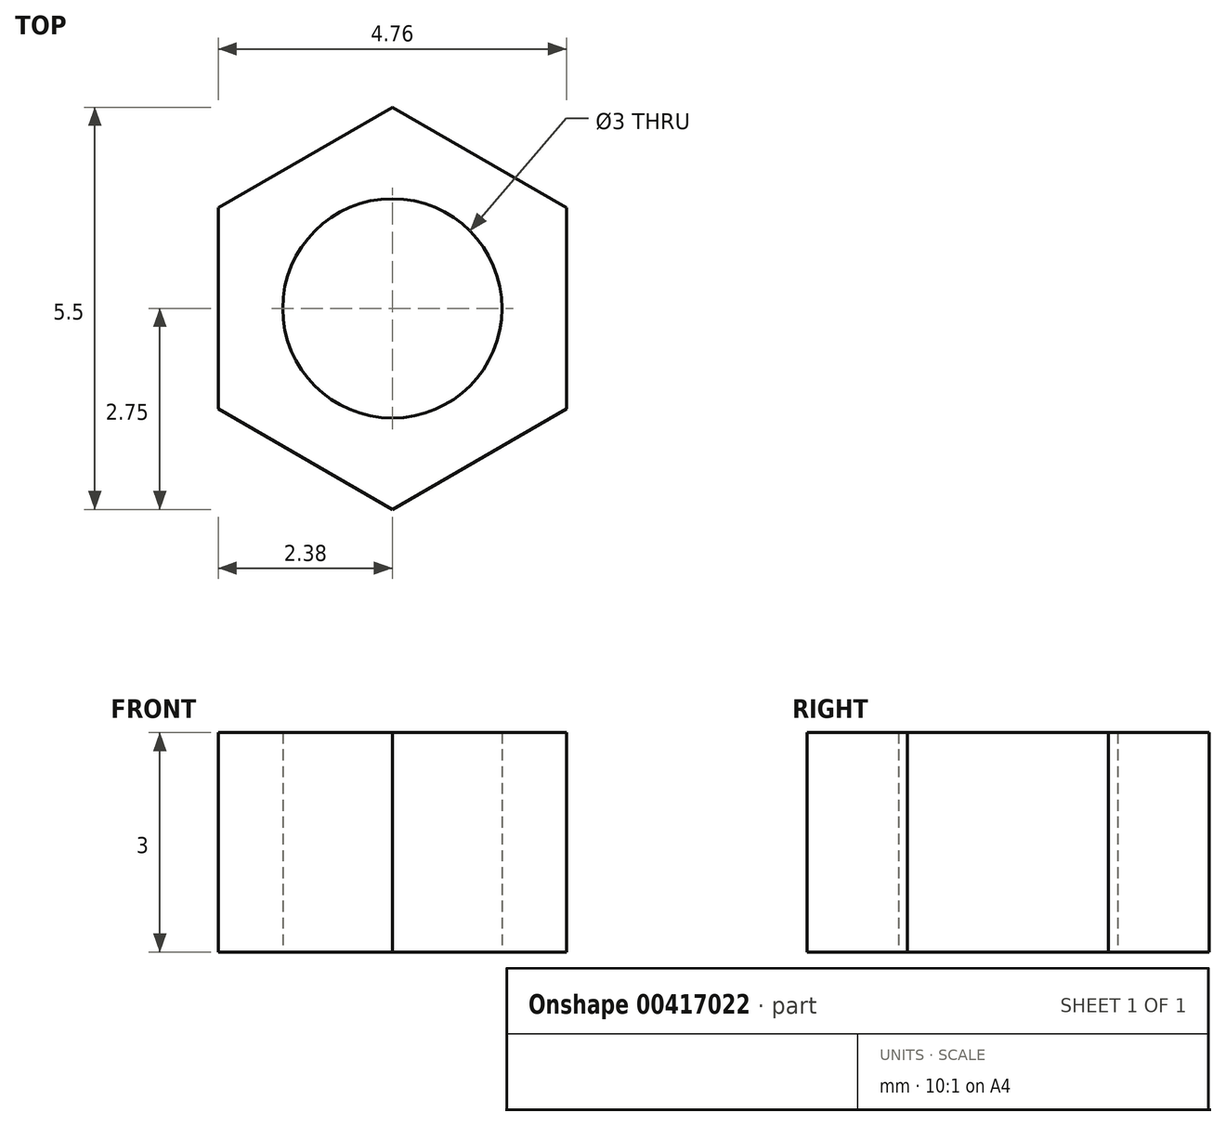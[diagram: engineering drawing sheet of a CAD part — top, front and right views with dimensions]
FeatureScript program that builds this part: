
annotation { "Feature Type Name" : "Feature", "Feature Type Description" : "" }
export const myFeature = defineFeature(function(context is Context, id is Id, definition is map)
    precondition{}
    {
        {
            var Q0;
            Q0=qCreatedBy(makeId("Top.planeOp"),FACE);
            var sketch = newSketch(context, id + "F0", { "sketchPlane" : qUnion([Q0])});
            skCircle(sketch, "E0.cCircle", {"center": v(0, 0) * mm, "radius": 2.38 * mm, "construction": true});
            skLineSegment(sketch, "E0.0", {"start": v(2.38, 1.37) * mm, "end": v(2.38, -1.37) * mm});
            skLineSegment(sketch, "E0.1", {"start": v(2.38, -1.37) * mm, "end": v(0, -2.75) * mm});
            skLineSegment(sketch, "E0.2", {"start": v(0, -2.75) * mm, "end": v(-2.38, -1.38) * mm});
            skLineSegment(sketch, "E0.3", {"start": v(-2.38, -1.38) * mm, "end": v(-2.38, 1.37) * mm});
            skLineSegment(sketch, "E0.4", {"start": v(-2.38, 1.37) * mm, "end": v(0, 2.75) * mm});
            skLineSegment(sketch, "E0.5", {"start": v(0, 2.75) * mm, "end": v(2.38, 1.37) * mm});
            skPoint(sketch, "E0.0.midPoint", {"position": v(2.38, 0) * mm});
            skCircle(sketch, "E1", {"center": v(0, 0) * mm, "radius": 1.5 * mm});
            skSolve(sketch);
        }
        {
            var Q0;
            Q0=makeQuery(id+"F0.imprint","IMPRINT",FACE,{"disambiguationData":[TD([[makeQuery(id+"F0.imprint","IMPRINT",EDGE,{"derivedFrom":sQuery(id+"F0.wireOp",EDGE,"E0.0")}),-1.0]])]});
            extrude(context, id + "F1", {"entities" : qUnion([Q0]), "depth" : 3 * mm});
        }
    });
